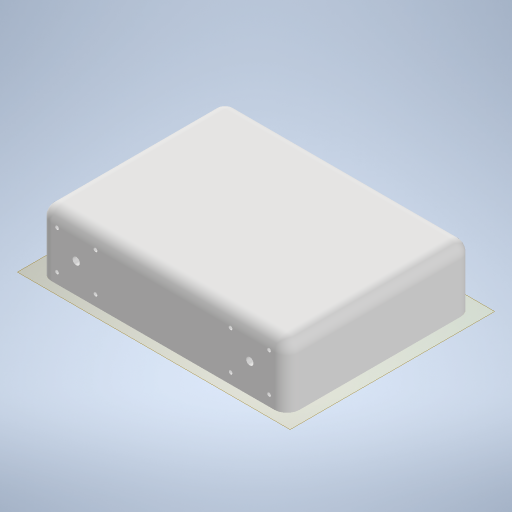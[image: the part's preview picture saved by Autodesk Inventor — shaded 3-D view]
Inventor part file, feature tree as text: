
AUTODESK INVENTOR PART (.ipt)
format: ipt  version: 2024 (Build 280153000, 153)  size: 317,440 bytes
history: native  units: mm
features: extrude x3, mirror x3, sketch x3, other x3, plane x1, fillet x1, reference x1, projected_geometry x1
ambient origin geometry x8: Origin, YZ Plane, XZ Plane, XY Plane, X Axis, Y Axis, Z Axis, Center Point
bodies: Solid1 (feature_tree)
feature tree (16):
  plane  "Work Plane1"
  extrude  "Extrusion1"  Depth=45.0mm TaperAngle=0.0deg
  extrude  "Extrusion2"  Depth=31.0mm
  extrude  "Extrusion3"  Depth=10.0mm
  mirror  "Mirror1"
  mirror  "Mirror2"
  mirror  "Mirror3"
  fillet  "Fillet1"  Radius=3.0mm
  sketch  "Sketch1"  dims[d0=5.0mm d1=45.0mm d2=0.0mm]
  reference  "Reference1"
  sketch  "Sketch2"  dims[d3=5.0mm d4=0.0mm d5=31.0mm]
  projected_geometry  "Projected Loop1"
  sketch  "Sketch3"  dims[d6=31.0mm d9=10.5mm d10=3.0mm d11=3.0mm d12=3.0mm d13=3.0mm d14=5.0mm d15=0.0mm d16=6.0mm d17=10.0mm d18=30.0mm d19=0.0mm d20=0.0mm]
  other  "<userpath> windows\Documents\Inventor\Robotska_roka\Assembly4.iam"
  other  "Assembly4.iam"
  other  "vozicek1:1"
